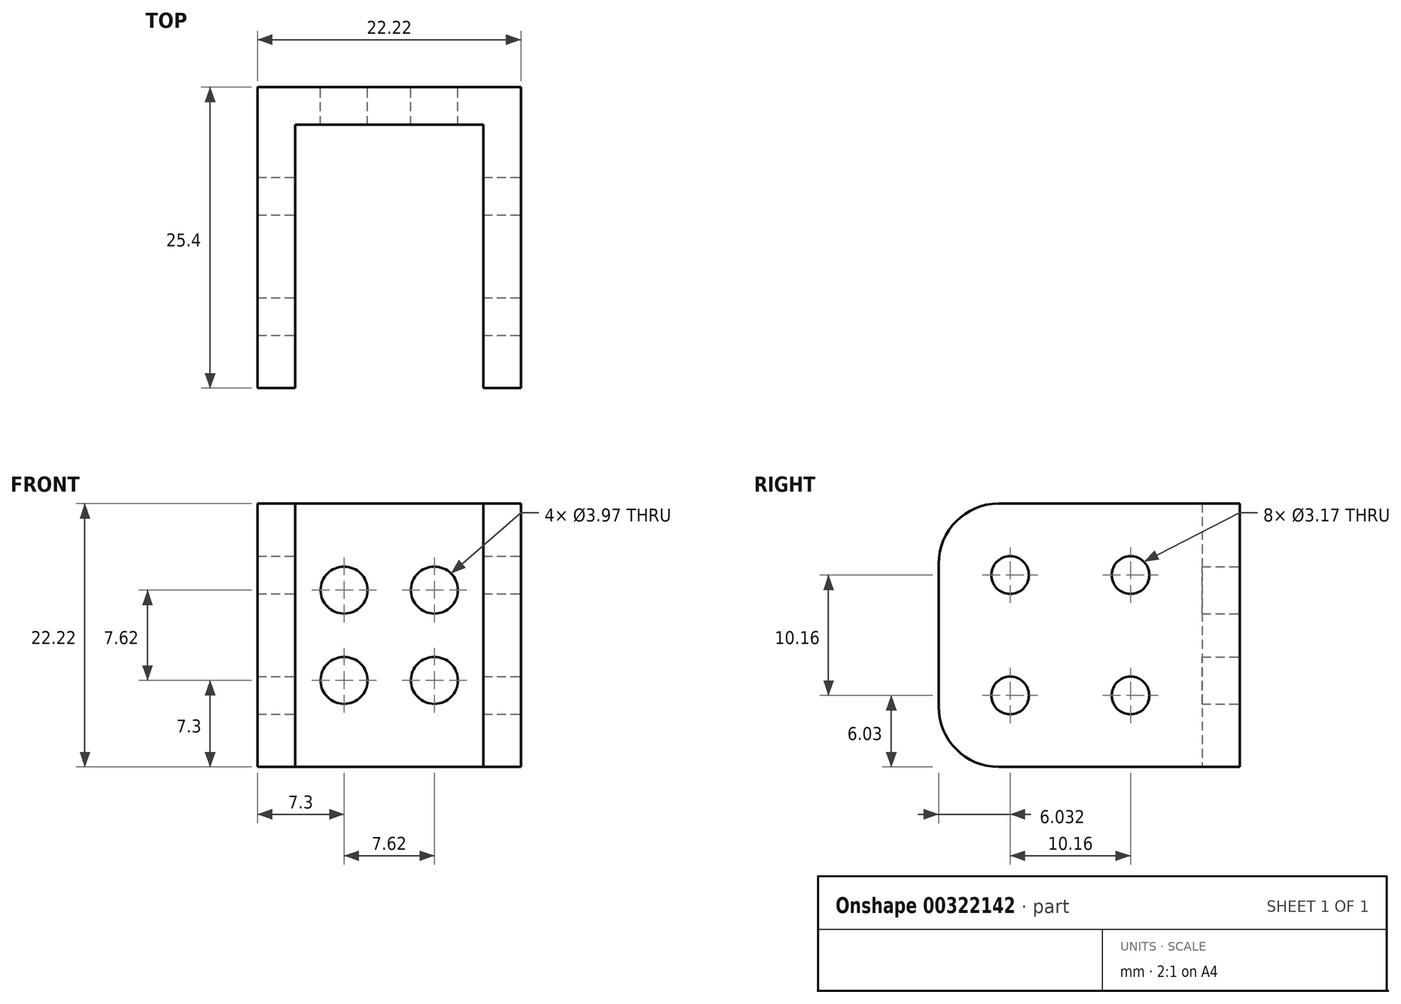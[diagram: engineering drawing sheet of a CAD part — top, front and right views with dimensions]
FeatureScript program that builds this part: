
annotation { "Feature Type Name" : "Feature", "Feature Type Description" : "" }
export const myFeature = defineFeature(function(context is Context, id is Id, definition is map)
    precondition{}
    {
        {
            var Q0;
            Q0=qCreatedBy(makeId("Front.planeOp"),FACE);
            var sketch = newSketch(context, id + "F0", { "sketchPlane" : qUnion([Q0])});
            skLineSegment(sketch, "E0.bottom", {"start": v(11.11, -11.11) * mm, "end": v(-11.11, -11.11) * mm});
            skLineSegment(sketch, "E0.top", {"start": v(11.11, 11.11) * mm, "end": v(-11.11, 11.11) * mm});
            skLineSegment(sketch, "E0.left", {"start": v(11.11, -11.11) * mm, "end": v(11.11, 11.11) * mm});
            skLineSegment(sketch, "E0.right", {"start": v(-11.11, -11.11) * mm, "end": v(-11.11, 11.11) * mm});
            skPoint(sketch, "E0.middle", {"position": v(0, 0) * mm});
            skCircle(sketch, "E1", {"center": v(-3.8, 3.81) * mm, "radius": 1.98 * mm});
            skCircle(sketch, "E2.0.1.0", {"center": v(-3.8, -3.81) * mm, "radius": 1.98 * mm});
            skCircle(sketch, "E2.1.0.0", {"center": v(3.8, 3.81) * mm, "radius": 1.98 * mm});
            skCircle(sketch, "E2.1.1.0", {"center": v(3.8, -3.81) * mm, "radius": 1.98 * mm});
            skLineSegment(sketch, "E2.direction1", {"start": v(-3.8, 3.81) * mm, "end": v(3.81, 3.81) * mm, "construction": true});
            skLineSegment(sketch, "E2.direction2", {"start": v(-3.81, 3.81) * mm, "end": v(-3.81, -3.81) * mm, "construction": true});
            skLineSegment(sketch, "E3", {"start": v(-7.94, 11.11) * mm, "end": v(-7.94, -11.11) * mm});
            skLineSegment(sketch, "E4", {"start": v(7.94, 11.11) * mm, "end": v(7.94, -11.11) * mm});
            skSolve(sketch);
        }
        {
            var Q0;
            Q0=makeQuery(id+"F0.imprint","IMPRINT",FACE,{"disambiguationData":[TD([[makeQuery(id+"F0.imprint","IMPRINT",EDGE,{"derivedFrom":sQuery(id+"F0.wireOp",EDGE,"E1")}),-1.0]])]});
            extrude(context, id + "F1", {"entities" : qUnion([Q0]), "depth" : 3.17 * mm});
        }
        {
            var Q0;
            {var subQ0=sQuery(id+"F0.wireOp",EDGE,"E0.left");Q0=makeQuery(id+"F0.imprint","IMPRINT",FACE,{"disambiguationData":[TD([[makeQuery(id+"F0.imprint","IMPRINT",EDGE,{"derivedFrom":subQ0}),1.0]])]});}
            var Q1;
            {var subQ0=sQuery(id+"F0.wireOp",EDGE,"E0.right");Q1=makeQuery(id+"F0.imprint","IMPRINT",FACE,{"disambiguationData":[TD([[makeQuery(id+"F0.imprint","IMPRINT",EDGE,{"derivedFrom":subQ0}),-1.0]])]});}
            extrude(context, id + "F2", {"entities" : qUnion([Q0, Q1]), "operationType" : NewBodyOperationType.ADD, "depth" : 25.4 * mm});
        }
        {
            var Q0;
            Q0=makeQuery(id+"F2.opExtrude","SWEPT_FACE",FACE,{"disambiguationData":[OSD([sQuery(id+"F0.wireOp",EDGE,"E0.left")])]});
            var sketch = newSketch(context, id + "F3", { "sketchPlane" : qUnion([Q0])});
            skLineSegment(sketch, "E5", {"start": v(-3.18, 11.11) * mm, "end": v(-3.17, -11.11) * mm});
            skLineSegment(sketch, "E6", {"start": v(-3.18, 11.11) * mm, "end": v(-25.4, 11.11) * mm, "construction": true});
            skLineSegment(sketch, "E7", {"start": v(-25.4, 11.11) * mm, "end": v(-25.4, -11.11) * mm, "construction": true});
            skLineSegment(sketch, "E8", {"start": v(-14.29, 11.11) * mm, "end": v(-14.29, -11.11) * mm, "construction": true});
            skLineSegment(sketch, "E9", {"start": v(-25.4, 0) * mm, "end": v(-3.18, 0) * mm, "construction": true});
            skCircle(sketch, "E10", {"center": v(-19.37, 5.08) * mm, "radius": 1.59 * mm});
            skCircle(sketch, "E11.1.0", {"center": v(-19.37, -5.08) * mm, "radius": 1.59 * mm});
            skCircle(sketch, "E11.2.0", {"center": v(-9.2, -5.08) * mm, "radius": 1.59 * mm});
            skCircle(sketch, "E11.3.0", {"center": v(-9.2, 5.08) * mm, "radius": 1.59 * mm});
            skPoint(sketch, "E11.center", {"position": v(-14.29, 0) * mm});
            skSolve(sketch);
        }
        {
            var Q0;
            Q0=makeQuery(id+"F3.imprint","IMPRINT",FACE,{"disambiguationData":[TD([[makeQuery(id+"F3.imprint","IMPRINT",EDGE,{"derivedFrom":sQuery(id+"F3.wireOp",EDGE,"E10")}),1.0]])]});
            var Q1;
            Q1=makeQuery(id+"F3.imprint","IMPRINT",FACE,{"disambiguationData":[TD([[makeQuery(id+"F3.imprint","IMPRINT",EDGE,{"derivedFrom":sQuery(id+"F3.wireOp",EDGE,"E11.3.0")}),1.0]])]});
            var Q2;
            Q2=makeQuery(id+"F3.imprint","IMPRINT",FACE,{"disambiguationData":[TD([[makeQuery(id+"F3.imprint","IMPRINT",EDGE,{"derivedFrom":sQuery(id+"F3.wireOp",EDGE,"E11.2.0")}),1.0]])]});
            var Q3;
            Q3=makeQuery(id+"F3.imprint","IMPRINT",FACE,{"disambiguationData":[TD([[makeQuery(id+"F3.imprint","IMPRINT",EDGE,{"derivedFrom":sQuery(id+"F3.wireOp",EDGE,"E11.1.0")}),1.0]])]});
            extrude(context, id + "F4", {"entities" : qUnion([Q0, Q1, Q2, Q3]), "operationType" : NewBodyOperationType.REMOVE, "endBound" : BoundingType.THROUGH_ALL, "oppositeDirection" : true, "depth" : 25.4 * mm});
        }
        {
            var Q0;
            {var subQ0=sQuery(id+"F0.wireOp",EDGE,"E0.top");Q0=makeQuery(id+"F2.opExtrude","CAP_EDGE",EDGE,{"disambiguationData":[OSD([subQ0]),TDD([makeQuery(id+"F0.imprint","IMPRINT",EDGE,{"disambiguationData":[TD([[makeQuery(id+"F0.imprint","INTERSECT",VERTEX,{"derivedFrom":[subQ0,sQuery(id+"F0.wireOp",EDGE,"E0.left")]}),-1.0]])],"derivedFrom":subQ0})])],"isStart":false});}
            var Q1;
            {var subQ0=sQuery(id+"F0.wireOp",EDGE,"E0.top");Q1=makeQuery(id+"F2.opExtrude","CAP_EDGE",EDGE,{"disambiguationData":[OSD([subQ0]),TDD([makeQuery(id+"F0.imprint","IMPRINT",EDGE,{"disambiguationData":[TD([[makeQuery(id+"F0.imprint","INTERSECT",VERTEX,{"derivedFrom":[subQ0,sQuery(id+"F0.wireOp",EDGE,"E0.right")]}),1.0]])],"derivedFrom":subQ0})])],"isStart":false});}
            var Q2;
            {var subQ0=sQuery(id+"F0.wireOp",EDGE,"E0.bottom");Q2=makeQuery(id+"F2.opExtrude","CAP_EDGE",EDGE,{"disambiguationData":[OSD([subQ0]),TDD([makeQuery(id+"F0.imprint","IMPRINT",EDGE,{"disambiguationData":[TD([[makeQuery(id+"F0.imprint","INTERSECT",VERTEX,{"derivedFrom":[subQ0,sQuery(id+"F0.wireOp",EDGE,"E0.left")]}),-1.0]])],"derivedFrom":subQ0})])],"isStart":false});}
            var Q3;
            {var subQ0=sQuery(id+"F0.wireOp",EDGE,"E0.bottom");Q3=makeQuery(id+"F2.opExtrude","CAP_EDGE",EDGE,{"disambiguationData":[OSD([subQ0]),TDD([makeQuery(id+"F0.imprint","IMPRINT",EDGE,{"disambiguationData":[TD([[makeQuery(id+"F0.imprint","INTERSECT",VERTEX,{"derivedFrom":[subQ0,sQuery(id+"F0.wireOp",EDGE,"E0.right")]}),1.0]])],"derivedFrom":subQ0})])],"isStart":false});}
            fillet(context, id + "F5", {"entities" : qUnion([Q0, Q1, Q2, Q3]), "radius" : 5.08 * mm, "tangentPropagation" : true, "allowEdgeOverflow" : false});
        }
    });
